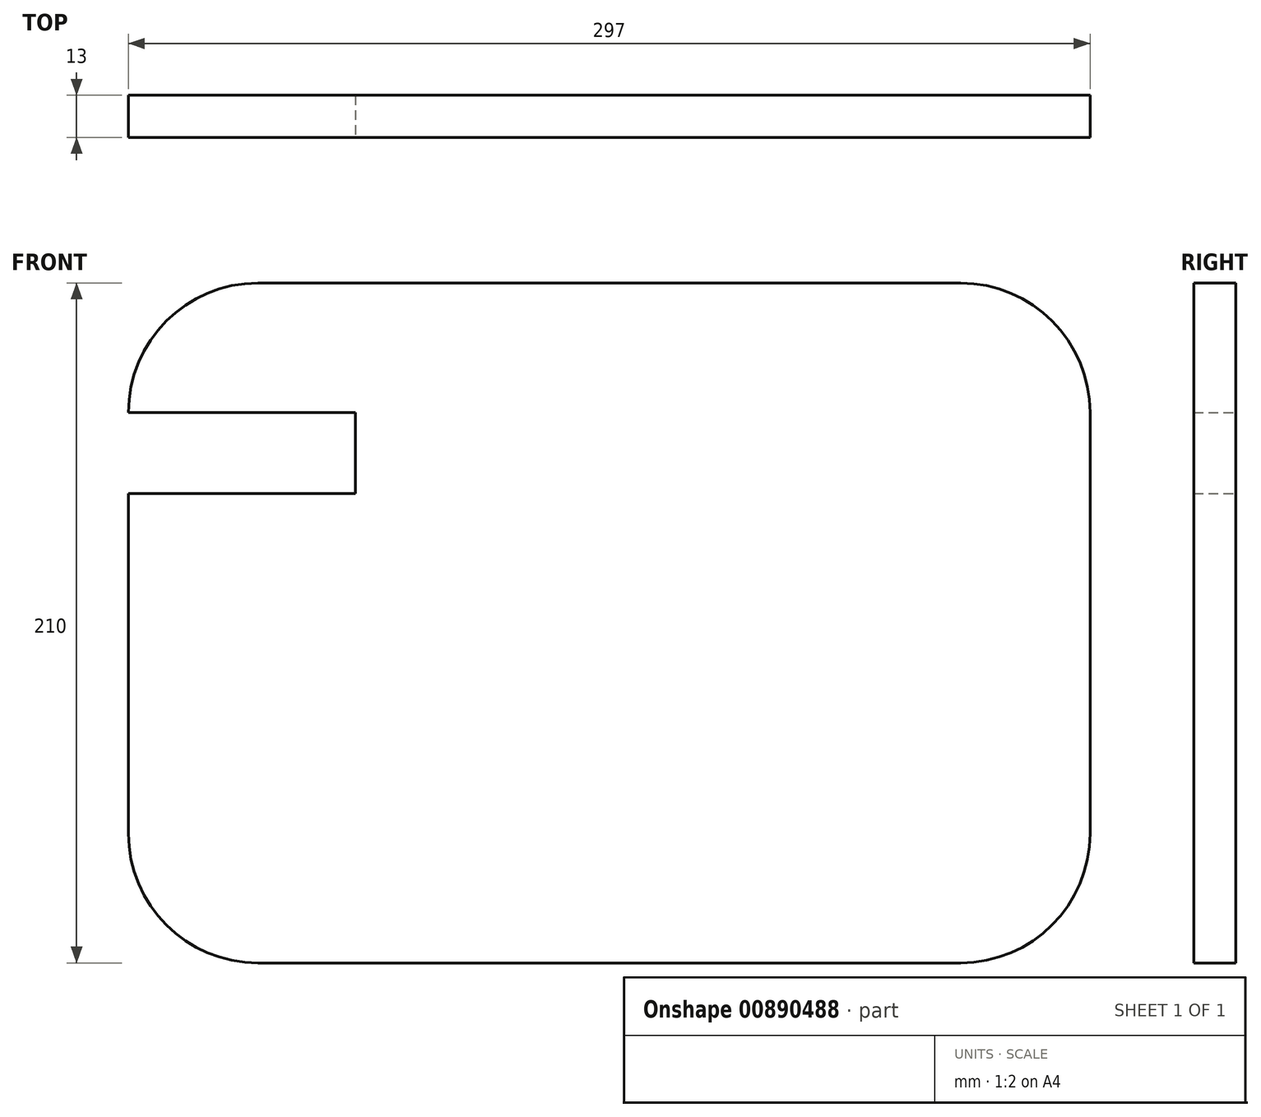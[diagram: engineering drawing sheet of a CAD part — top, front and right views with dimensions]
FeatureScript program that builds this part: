
annotation { "Feature Type Name" : "Feature", "Feature Type Description" : "" }
export const myFeature = defineFeature(function(context is Context, id is Id, definition is map)
    precondition{}
    {
        {
            var Q0;
            Q0=qCreatedBy(makeId("Front.planeOp"),FACE);
            var sketch = newSketch(context, id + "F0", { "sketchPlane" : qUnion([Q0])});
            skLineSegment(sketch, "E0.bottom", {"start": v(-71.93, 99.4) * mm, "end": v(145.07, 99.4) * mm});
            skLineSegment(sketch, "E0.top", {"start": v(-71.93, -110.6) * mm, "end": v(145.07, -110.6) * mm});
            skLineSegment(sketch, "E0.left", {"start": v(-111.93, 59.4) * mm, "end": v(-111.93, -70.6) * mm});
            skLineSegment(sketch, "E0.right", {"start": v(185.07, 59.4) * mm, "end": v(185.07, -70.6) * mm});
            skPoint(sketch, "E1.visualSharp", {"position": v(185.07, 99.4) * mm});
            skArc(sketch, "E1.filletArc", {"start": v(185.07, 59.4) * mm, "mid": v(173.35, 87.69) * mm, "end": v(145.07, 99.4) * mm});
            skPoint(sketch, "E2.visualSharp", {"position": v(-111.93, 99.4) * mm});
            skArc(sketch, "E2.filletArc", {"start": v(-71.93, 99.4) * mm, "mid": v(-100.22, 87.69) * mm, "end": v(-111.93, 59.4) * mm});
            skPoint(sketch, "E3.visualSharp", {"position": v(-111.93, -110.6) * mm});
            skArc(sketch, "E3.filletArc", {"start": v(-111.93, -70.6) * mm, "mid": v(-100.22, -98.88) * mm, "end": v(-71.93, -110.6) * mm});
            skPoint(sketch, "E4.visualSharp", {"position": v(185.07, -110.6) * mm});
            skArc(sketch, "E4.filletArc", {"start": v(145.07, -110.6) * mm, "mid": v(173.35, -98.88) * mm, "end": v(185.07, -70.6) * mm});
            skSolve(sketch);
        }
        {
            var Q0;
            Q0=makeQuery(id+"F0.imprint","IMPRINT",FACE,{"disambiguationData":[TD([[makeQuery(id+"F0.imprint","IMPRINT",EDGE,{"derivedFrom":sQuery(id+"F0.wireOp",EDGE,"E0.bottom")}),-1.0]])]});
            extrude(context, id + "F1", {"entities" : qUnion([Q0]), "depth" : 13 * mm, "offsetDistance" : 25 * mm});
        }
        {
            var Q0;
            Q0=makeQuery(id+"F1.opExtrude","CAP_FACE",FACE,{"disambiguationData":[OSD([sQuery(id+"F0.wireOp",EDGE,"E0.bottom"),sQuery(id+"F0.wireOp",EDGE,"E0.top"),sQuery(id+"F0.wireOp",EDGE,"E0.left"),sQuery(id+"F0.wireOp",EDGE,"E0.right"),sQuery(id+"F0.wireOp",EDGE,"E1.filletArc"),sQuery(id+"F0.wireOp",EDGE,"E2.filletArc"),sQuery(id+"F0.wireOp",EDGE,"E3.filletArc"),sQuery(id+"F0.wireOp",EDGE,"E4.filletArc")])],"isStart":false});
            var sketch = newSketch(context, id + "F2", { "sketchPlane" : qUnion([Q0])});
            skLineSegment(sketch, "E5.bottom", {"start": v(-116.88, 59.4) * mm, "end": v(-41.88, 59.4) * mm});
            skLineSegment(sketch, "E5.top", {"start": v(-116.88, 34.4) * mm, "end": v(-41.88, 34.4) * mm});
            skLineSegment(sketch, "E5.left", {"start": v(-116.88, 59.4) * mm, "end": v(-116.88, 34.4) * mm});
            skLineSegment(sketch, "E5.right", {"start": v(-41.88, 59.4) * mm, "end": v(-41.88, 34.4) * mm});
            skSolve(sketch);
        }
        {
            var Q0;
            Q0 = qSketchRegion(id + "F2", true);
            extrude(context, id + "F3", {"entities" : qUnion([Q0]), "operationType" : NewBodyOperationType.REMOVE, "oppositeDirection" : true, "depth" : 25 * mm, "offsetDistance" : 25 * mm});
        }
    });
